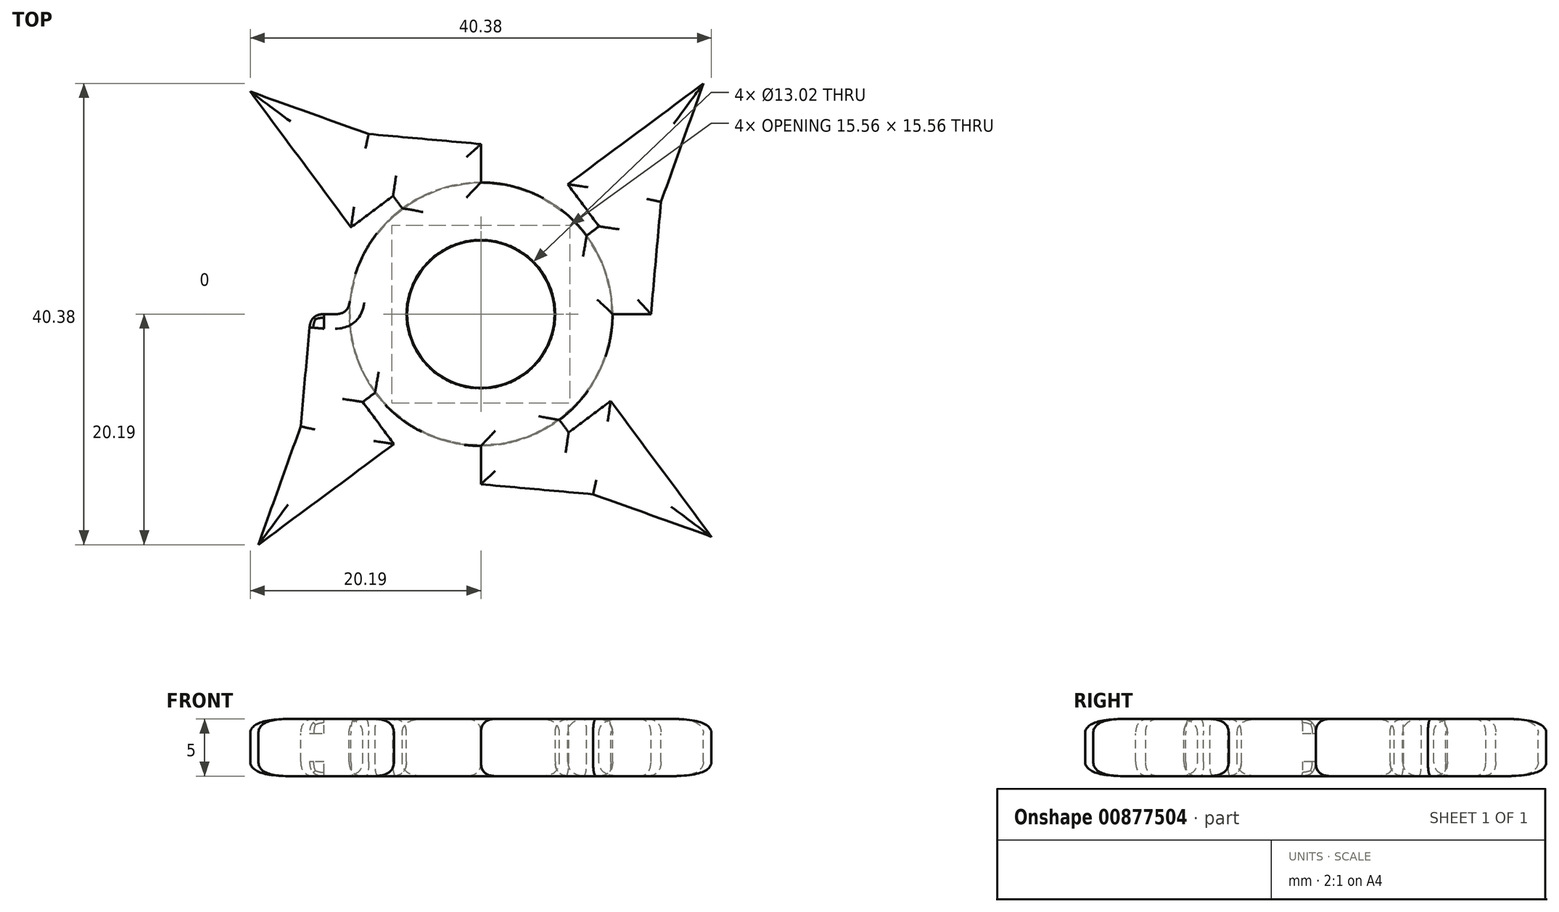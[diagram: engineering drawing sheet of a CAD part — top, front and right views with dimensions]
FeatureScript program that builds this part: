
annotation { "Feature Type Name" : "Feature", "Feature Type Description" : "" }
export const myFeature = defineFeature(function(context is Context, id is Id, definition is map)
    precondition{}
    {
        {
            var Q0;
            Q0=qCreatedBy(makeId("Top.planeOp"),FACE);
            var sketch = newSketch(context, id + "F0", { "sketchPlane" : qUnion([Q0])});
            skLineSegment(sketch, "E0", {"start": v(-7.68, 10.35) * mm, "end": v(0, 0) * mm});
            skLineSegment(sketch, "E1", {"start": v(0, 0) * mm, "end": v(0, 14.9) * mm});
            skCircle(sketch, "E2", {"center": v(0, 0) * mm, "radius": 11.54 * mm});
            skCircle(sketch, "E3", {"center": v(0, 0) * mm, "radius": 6.51 * mm});
            skLineSegment(sketch, "E4", {"start": v(-7.68, 10.35) * mm, "end": v(-11.37, 7.6) * mm});
            skLineSegment(sketch, "E5", {"start": v(-11.37, 7.6) * mm, "end": v(-20.19, 19.48) * mm});
            skLineSegment(sketch, "E6", {"start": v(-20.19, 19.48) * mm, "end": v(-9.82, 15.77) * mm});
            skLineSegment(sketch, "E7", {"start": v(-9.82, 15.77) * mm, "end": v(0, 14.9) * mm});
            skSolve(sketch);
        }
        {
            var Q0;
            Q0 = qSketchRegion(id + "F0", true);
            extrude(context, id + "F1", {"entities" : qUnion([Q0]), "oppositeDirection" : true, "depth" : 5 * mm, "offsetDistance" : 25.4 * mm});
        }
        {
            var Q0;
            Q0=qCreatedBy(makeId("Right.planeOp"),FACE);
            var sketch = newSketch(context, id + "F2", { "sketchPlane" : qUnion([Q0])});
            skLineSegment(sketch, "E8", {"start": v(0, 77.41) * mm, "end": v(0, -76.13) * mm});
            skSolve(sketch);
        }
        {
            var Q0;
            Q0=makeQuery(id+"F1.opExtrude","SWEPT_BODY",BODY,{"disambiguationData":[OSD([sQuery(id+"F0.wireOp",EDGE,"peLfI5ue-QDtm-64uR-NCye-FpjKrs892AIN"),sQuery(id+"F0.wireOp",EDGE,"XeauMBtL-qSNJ-Du5e-MjSf-suMh1z73021i"),sQuery(id+"F0.wireOp",EDGE,"uCkJ3IbV-9PuM-OyKt-12wW-s1nBjEn3Bnat"),sQuery(id+"F0.wireOp",EDGE,"jbe7xcwy-JMVv-QHlx-iZXR-E8UkWCgJ8VfW"),sQuery(id+"F0.wireOp",EDGE,"xrz1sUs9-kp8S-nQkl-THXK-nKrd9pMfuxZ6"),sQuery(id+"F0.wireOp",EDGE,"ltCTPJuN-vA8q-3FSW-viVL-nSudp19Bd019"),sQuery(id+"F0.wireOp",EDGE,"J34Ahusi-QFJQ-7KdZ-FfkN-kxVdJVjI1dXk"),sQuery(id+"F0.wireOp",EDGE,"wvHOoMUv-5DXu-3SaJ-NkCi-idFzraKzYJUX"),sQuery(id+"F0.wireOp",EDGE,"I4517xHe-oppO-bLI7-yov1-ZNSnUnbMDINO"),sQuery(id+"F0.wireOp",EDGE,"E0"),sQuery(id+"F0.wireOp",EDGE,"E1"),sQuery(id+"F0.wireOp",EDGE,"aFCqyNYx-4qZV-YJUx-UeDV-WOpdEz68UfCI")])]});
            var Q1;
            Q1=sQuery(id+"F2.wireOp",EDGE,"E8");
            circularPattern(context, id + "F3", {"entities" : qUnion([Q0]), "axis" : qUnion([Q1]), "angle" : 360 * degree, "instanceCount" : 4, "oppositeDirection" : true, "equalSpace" : true});
        }
        {
            var Q0;
            Q0=makeQuery(id+"F3.opPattern","COPY",FACE,{"derivedFrom":makeQuery(id+"F1.opExtrude","CAP_FACE",FACE,{"disambiguationData":[OSD([sQuery(id+"F0.wireOp",EDGE,"peLfI5ue-QDtm-64uR-NCye-FpjKrs892AIN"),sQuery(id+"F0.wireOp",EDGE,"XeauMBtL-qSNJ-Du5e-MjSf-suMh1z73021i"),sQuery(id+"F0.wireOp",EDGE,"uCkJ3IbV-9PuM-OyKt-12wW-s1nBjEn3Bnat"),sQuery(id+"F0.wireOp",EDGE,"jbe7xcwy-JMVv-QHlx-iZXR-E8UkWCgJ8VfW"),sQuery(id+"F0.wireOp",EDGE,"xrz1sUs9-kp8S-nQkl-THXK-nKrd9pMfuxZ6"),sQuery(id+"F0.wireOp",EDGE,"ltCTPJuN-vA8q-3FSW-viVL-nSudp19Bd019"),sQuery(id+"F0.wireOp",EDGE,"J34Ahusi-QFJQ-7KdZ-FfkN-kxVdJVjI1dXk"),sQuery(id+"F0.wireOp",EDGE,"wvHOoMUv-5DXu-3SaJ-NkCi-idFzraKzYJUX"),sQuery(id+"F0.wireOp",EDGE,"I4517xHe-oppO-bLI7-yov1-ZNSnUnbMDINO"),sQuery(id+"F0.wireOp",EDGE,"E0"),sQuery(id+"F0.wireOp",EDGE,"E1"),sQuery(id+"F0.wireOp",EDGE,"aFCqyNYx-4qZV-YJUx-UeDV-WOpdEz68UfCI"),sQuery(id+"F0.wireOp",EDGE,"E2"),sQuery(id+"F0.wireOp",EDGE,"E3")])],"isStart":false}),"instanceName":"2"});
            var Q1;
            Q1=makeQuery(id+"F3.opPattern","COPY",FACE,{"derivedFrom":makeQuery(id+"F1.opExtrude","CAP_FACE",FACE,{"disambiguationData":[OSD([sQuery(id+"F0.wireOp",EDGE,"peLfI5ue-QDtm-64uR-NCye-FpjKrs892AIN"),sQuery(id+"F0.wireOp",EDGE,"XeauMBtL-qSNJ-Du5e-MjSf-suMh1z73021i"),sQuery(id+"F0.wireOp",EDGE,"uCkJ3IbV-9PuM-OyKt-12wW-s1nBjEn3Bnat"),sQuery(id+"F0.wireOp",EDGE,"jbe7xcwy-JMVv-QHlx-iZXR-E8UkWCgJ8VfW"),sQuery(id+"F0.wireOp",EDGE,"xrz1sUs9-kp8S-nQkl-THXK-nKrd9pMfuxZ6"),sQuery(id+"F0.wireOp",EDGE,"ltCTPJuN-vA8q-3FSW-viVL-nSudp19Bd019"),sQuery(id+"F0.wireOp",EDGE,"J34Ahusi-QFJQ-7KdZ-FfkN-kxVdJVjI1dXk"),sQuery(id+"F0.wireOp",EDGE,"wvHOoMUv-5DXu-3SaJ-NkCi-idFzraKzYJUX"),sQuery(id+"F0.wireOp",EDGE,"I4517xHe-oppO-bLI7-yov1-ZNSnUnbMDINO"),sQuery(id+"F0.wireOp",EDGE,"E0"),sQuery(id+"F0.wireOp",EDGE,"E1"),sQuery(id+"F0.wireOp",EDGE,"aFCqyNYx-4qZV-YJUx-UeDV-WOpdEz68UfCI"),sQuery(id+"F0.wireOp",EDGE,"E2"),sQuery(id+"F0.wireOp",EDGE,"E3")])],"isStart":false}),"instanceName":"3"});
            var Q2;
            Q2=makeQuery(id+"F1.opExtrude","CAP_FACE",FACE,{"disambiguationData":[OSD([sQuery(id+"F0.wireOp",EDGE,"peLfI5ue-QDtm-64uR-NCye-FpjKrs892AIN"),sQuery(id+"F0.wireOp",EDGE,"XeauMBtL-qSNJ-Du5e-MjSf-suMh1z73021i"),sQuery(id+"F0.wireOp",EDGE,"uCkJ3IbV-9PuM-OyKt-12wW-s1nBjEn3Bnat"),sQuery(id+"F0.wireOp",EDGE,"jbe7xcwy-JMVv-QHlx-iZXR-E8UkWCgJ8VfW"),sQuery(id+"F0.wireOp",EDGE,"xrz1sUs9-kp8S-nQkl-THXK-nKrd9pMfuxZ6"),sQuery(id+"F0.wireOp",EDGE,"ltCTPJuN-vA8q-3FSW-viVL-nSudp19Bd019"),sQuery(id+"F0.wireOp",EDGE,"J34Ahusi-QFJQ-7KdZ-FfkN-kxVdJVjI1dXk"),sQuery(id+"F0.wireOp",EDGE,"wvHOoMUv-5DXu-3SaJ-NkCi-idFzraKzYJUX"),sQuery(id+"F0.wireOp",EDGE,"I4517xHe-oppO-bLI7-yov1-ZNSnUnbMDINO"),sQuery(id+"F0.wireOp",EDGE,"E0"),sQuery(id+"F0.wireOp",EDGE,"E1"),sQuery(id+"F0.wireOp",EDGE,"aFCqyNYx-4qZV-YJUx-UeDV-WOpdEz68UfCI"),sQuery(id+"F0.wireOp",EDGE,"E2"),sQuery(id+"F0.wireOp",EDGE,"E3")])],"isStart":false});
            var Q3;
            Q3=makeQuery(id+"F3.opPattern","COPY",FACE,{"derivedFrom":makeQuery(id+"F1.opExtrude","CAP_FACE",FACE,{"disambiguationData":[OSD([sQuery(id+"F0.wireOp",EDGE,"peLfI5ue-QDtm-64uR-NCye-FpjKrs892AIN"),sQuery(id+"F0.wireOp",EDGE,"XeauMBtL-qSNJ-Du5e-MjSf-suMh1z73021i"),sQuery(id+"F0.wireOp",EDGE,"uCkJ3IbV-9PuM-OyKt-12wW-s1nBjEn3Bnat"),sQuery(id+"F0.wireOp",EDGE,"jbe7xcwy-JMVv-QHlx-iZXR-E8UkWCgJ8VfW"),sQuery(id+"F0.wireOp",EDGE,"xrz1sUs9-kp8S-nQkl-THXK-nKrd9pMfuxZ6"),sQuery(id+"F0.wireOp",EDGE,"ltCTPJuN-vA8q-3FSW-viVL-nSudp19Bd019"),sQuery(id+"F0.wireOp",EDGE,"J34Ahusi-QFJQ-7KdZ-FfkN-kxVdJVjI1dXk"),sQuery(id+"F0.wireOp",EDGE,"wvHOoMUv-5DXu-3SaJ-NkCi-idFzraKzYJUX"),sQuery(id+"F0.wireOp",EDGE,"I4517xHe-oppO-bLI7-yov1-ZNSnUnbMDINO"),sQuery(id+"F0.wireOp",EDGE,"E0"),sQuery(id+"F0.wireOp",EDGE,"E1"),sQuery(id+"F0.wireOp",EDGE,"aFCqyNYx-4qZV-YJUx-UeDV-WOpdEz68UfCI"),sQuery(id+"F0.wireOp",EDGE,"E2"),sQuery(id+"F0.wireOp",EDGE,"E3")])],"isStart":false}),"instanceName":"1"});
            var Q4;
            Q4=makeQuery(id+"F3.opPattern","COPY",FACE,{"derivedFrom":makeQuery(id+"F1.opExtrude","CAP_FACE",FACE,{"disambiguationData":[OSD([sQuery(id+"F0.wireOp",EDGE,"peLfI5ue-QDtm-64uR-NCye-FpjKrs892AIN"),sQuery(id+"F0.wireOp",EDGE,"XeauMBtL-qSNJ-Du5e-MjSf-suMh1z73021i"),sQuery(id+"F0.wireOp",EDGE,"uCkJ3IbV-9PuM-OyKt-12wW-s1nBjEn3Bnat"),sQuery(id+"F0.wireOp",EDGE,"jbe7xcwy-JMVv-QHlx-iZXR-E8UkWCgJ8VfW"),sQuery(id+"F0.wireOp",EDGE,"xrz1sUs9-kp8S-nQkl-THXK-nKrd9pMfuxZ6"),sQuery(id+"F0.wireOp",EDGE,"ltCTPJuN-vA8q-3FSW-viVL-nSudp19Bd019"),sQuery(id+"F0.wireOp",EDGE,"J34Ahusi-QFJQ-7KdZ-FfkN-kxVdJVjI1dXk"),sQuery(id+"F0.wireOp",EDGE,"wvHOoMUv-5DXu-3SaJ-NkCi-idFzraKzYJUX"),sQuery(id+"F0.wireOp",EDGE,"I4517xHe-oppO-bLI7-yov1-ZNSnUnbMDINO"),sQuery(id+"F0.wireOp",EDGE,"E0"),sQuery(id+"F0.wireOp",EDGE,"E1"),sQuery(id+"F0.wireOp",EDGE,"aFCqyNYx-4qZV-YJUx-UeDV-WOpdEz68UfCI"),sQuery(id+"F0.wireOp",EDGE,"E2"),sQuery(id+"F0.wireOp",EDGE,"E3")])],"isStart":true}),"instanceName":"2"});
            var Q5;
            Q5=makeQuery(id+"F3.opPattern","COPY",FACE,{"derivedFrom":makeQuery(id+"F1.opExtrude","CAP_FACE",FACE,{"disambiguationData":[OSD([sQuery(id+"F0.wireOp",EDGE,"peLfI5ue-QDtm-64uR-NCye-FpjKrs892AIN"),sQuery(id+"F0.wireOp",EDGE,"XeauMBtL-qSNJ-Du5e-MjSf-suMh1z73021i"),sQuery(id+"F0.wireOp",EDGE,"uCkJ3IbV-9PuM-OyKt-12wW-s1nBjEn3Bnat"),sQuery(id+"F0.wireOp",EDGE,"jbe7xcwy-JMVv-QHlx-iZXR-E8UkWCgJ8VfW"),sQuery(id+"F0.wireOp",EDGE,"xrz1sUs9-kp8S-nQkl-THXK-nKrd9pMfuxZ6"),sQuery(id+"F0.wireOp",EDGE,"ltCTPJuN-vA8q-3FSW-viVL-nSudp19Bd019"),sQuery(id+"F0.wireOp",EDGE,"J34Ahusi-QFJQ-7KdZ-FfkN-kxVdJVjI1dXk"),sQuery(id+"F0.wireOp",EDGE,"wvHOoMUv-5DXu-3SaJ-NkCi-idFzraKzYJUX"),sQuery(id+"F0.wireOp",EDGE,"I4517xHe-oppO-bLI7-yov1-ZNSnUnbMDINO"),sQuery(id+"F0.wireOp",EDGE,"E0"),sQuery(id+"F0.wireOp",EDGE,"E1"),sQuery(id+"F0.wireOp",EDGE,"aFCqyNYx-4qZV-YJUx-UeDV-WOpdEz68UfCI"),sQuery(id+"F0.wireOp",EDGE,"E2"),sQuery(id+"F0.wireOp",EDGE,"E3")])],"isStart":true}),"instanceName":"3"});
            var Q6;
            Q6=makeQuery(id+"F1.opExtrude","CAP_FACE",FACE,{"disambiguationData":[OSD([sQuery(id+"F0.wireOp",EDGE,"peLfI5ue-QDtm-64uR-NCye-FpjKrs892AIN"),sQuery(id+"F0.wireOp",EDGE,"XeauMBtL-qSNJ-Du5e-MjSf-suMh1z73021i"),sQuery(id+"F0.wireOp",EDGE,"uCkJ3IbV-9PuM-OyKt-12wW-s1nBjEn3Bnat"),sQuery(id+"F0.wireOp",EDGE,"jbe7xcwy-JMVv-QHlx-iZXR-E8UkWCgJ8VfW"),sQuery(id+"F0.wireOp",EDGE,"xrz1sUs9-kp8S-nQkl-THXK-nKrd9pMfuxZ6"),sQuery(id+"F0.wireOp",EDGE,"ltCTPJuN-vA8q-3FSW-viVL-nSudp19Bd019"),sQuery(id+"F0.wireOp",EDGE,"J34Ahusi-QFJQ-7KdZ-FfkN-kxVdJVjI1dXk"),sQuery(id+"F0.wireOp",EDGE,"wvHOoMUv-5DXu-3SaJ-NkCi-idFzraKzYJUX"),sQuery(id+"F0.wireOp",EDGE,"I4517xHe-oppO-bLI7-yov1-ZNSnUnbMDINO"),sQuery(id+"F0.wireOp",EDGE,"E0"),sQuery(id+"F0.wireOp",EDGE,"E1"),sQuery(id+"F0.wireOp",EDGE,"aFCqyNYx-4qZV-YJUx-UeDV-WOpdEz68UfCI"),sQuery(id+"F0.wireOp",EDGE,"E2"),sQuery(id+"F0.wireOp",EDGE,"E3")])],"isStart":true});
            var Q7;
            Q7=makeQuery(id+"F1.opExtrude","CAP_EDGE",EDGE,{"disambiguationData":[OSD([sQuery(id+"F0.wireOp",EDGE,"E3")])],"isStart":true});
            var Q8;
            Q8=makeQuery(id+"F3.opPattern","COPY",FACE,{"derivedFrom":makeQuery(id+"F1.opExtrude","CAP_FACE",FACE,{"disambiguationData":[OSD([sQuery(id+"F0.wireOp",EDGE,"peLfI5ue-QDtm-64uR-NCye-FpjKrs892AIN"),sQuery(id+"F0.wireOp",EDGE,"XeauMBtL-qSNJ-Du5e-MjSf-suMh1z73021i"),sQuery(id+"F0.wireOp",EDGE,"uCkJ3IbV-9PuM-OyKt-12wW-s1nBjEn3Bnat"),sQuery(id+"F0.wireOp",EDGE,"jbe7xcwy-JMVv-QHlx-iZXR-E8UkWCgJ8VfW"),sQuery(id+"F0.wireOp",EDGE,"xrz1sUs9-kp8S-nQkl-THXK-nKrd9pMfuxZ6"),sQuery(id+"F0.wireOp",EDGE,"ltCTPJuN-vA8q-3FSW-viVL-nSudp19Bd019"),sQuery(id+"F0.wireOp",EDGE,"J34Ahusi-QFJQ-7KdZ-FfkN-kxVdJVjI1dXk"),sQuery(id+"F0.wireOp",EDGE,"wvHOoMUv-5DXu-3SaJ-NkCi-idFzraKzYJUX"),sQuery(id+"F0.wireOp",EDGE,"I4517xHe-oppO-bLI7-yov1-ZNSnUnbMDINO"),sQuery(id+"F0.wireOp",EDGE,"E0"),sQuery(id+"F0.wireOp",EDGE,"E1"),sQuery(id+"F0.wireOp",EDGE,"aFCqyNYx-4qZV-YJUx-UeDV-WOpdEz68UfCI"),sQuery(id+"F0.wireOp",EDGE,"E2"),sQuery(id+"F0.wireOp",EDGE,"E3")])],"isStart":true}),"instanceName":"1"});
            var Q9;
            Q9=makeQuery(id+"F3.opPattern","COPY",FACE,{"derivedFrom":makeQuery(id+"F1.opExtrude","SWEPT_FACE",FACE,{"disambiguationData":[OSD([sQuery(id+"F0.wireOp",EDGE,"peLfI5ue-QDtm-64uR-NCye-FpjKrs892AIN")])]}),"instanceName":"1"});
            var Q10;
            Q10=makeQuery(id+"F3.opPattern","COPY",FACE,{"derivedFrom":makeQuery(id+"F1.opExtrude","SWEPT_FACE",FACE,{"disambiguationData":[OSD([sQuery(id+"F0.wireOp",EDGE,"E1")])]}),"instanceName":"1"});
            fillet(context, id + "F4", {"entities" : qUnion([Q0, Q1, Q2, Q3, Q4, Q5, Q6, Q7, Q8, Q9, Q10]), "radius" : 1.27 * mm, "tangentPropagation" : true, "rho" : 0.5, "crossSection" : FilletCrossSection.CONIC, "allowEdgeOverflow" : false});
        }
    });
